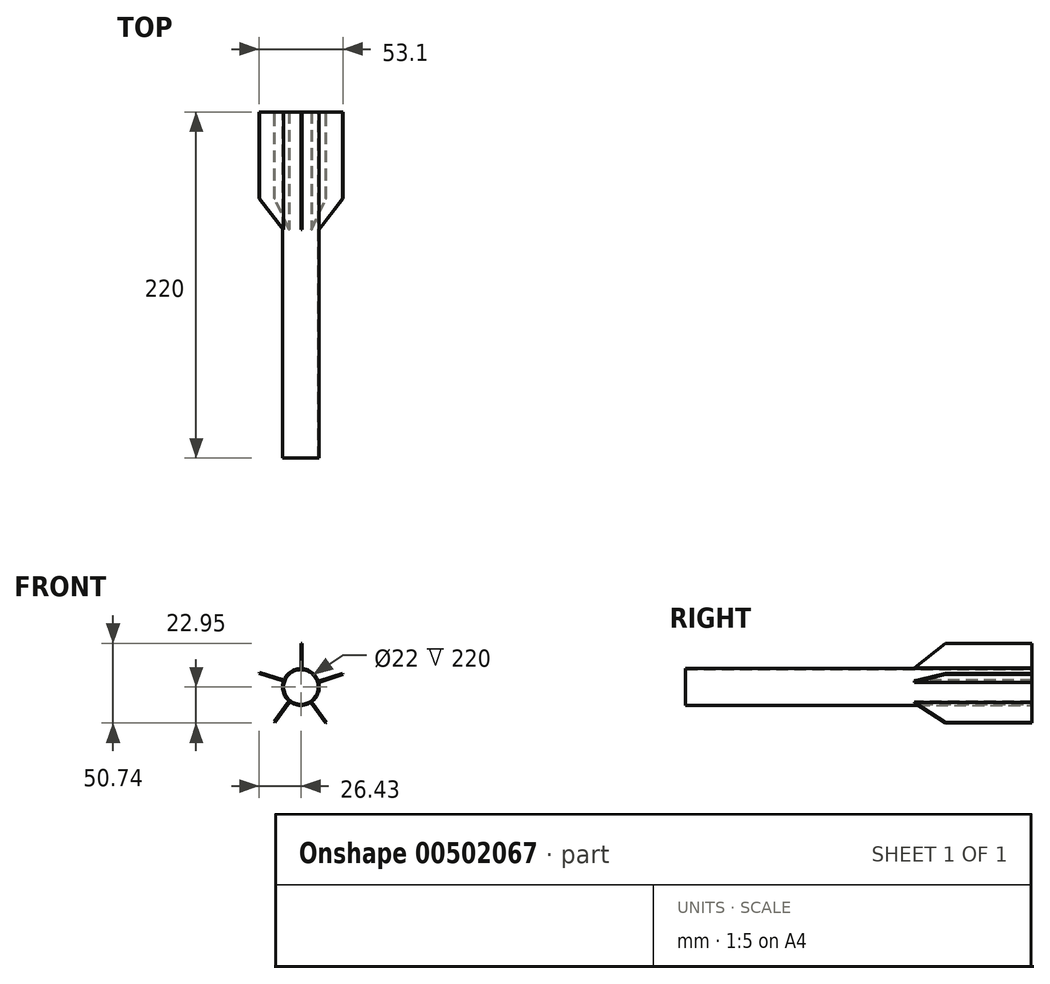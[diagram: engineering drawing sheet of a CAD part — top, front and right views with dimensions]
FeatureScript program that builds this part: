
annotation { "Feature Type Name" : "Feature", "Feature Type Description" : "" }
export const myFeature = defineFeature(function(context is Context, id is Id, definition is map)
    precondition{}
    {
        {
            var Q0;
            Q0=qCreatedBy(makeId("Front.planeOp"),FACE);
            var sketch = newSketch(context, id + "F0", { "sketchPlane" : qUnion([Q0])});
            skCircle(sketch, "E0", {"center": v(0, 0) * mm, "radius": 11.65 * mm});
            skCircle(sketch, "E1", {"center": v(0, 0) * mm, "radius": 11 * mm});
            skSolve(sketch);
        }
        {
            var Q0;
            Q0=makeQuery(id+"F0.imprint","IMPRINT",FACE,{"disambiguationData":[TD([[makeQuery(id+"F0.imprint","IMPRINT",EDGE,{"derivedFrom":sQuery(id+"F0.wireOp",EDGE,"E0")}),1.0]])]});
            extrude(context, id + "F1", {"entities" : qUnion([Q0]), "depth" : 220 * mm});
        }
        {
            var Q0;
            Q0=qCreatedBy(makeId("Right.planeOp"),FACE);
            var sketch = newSketch(context, id + "F2", { "sketchPlane" : qUnion([Q0])});
            skLineSegment(sketch, "E2", {"start": v(0, 11.98) * mm, "end": v(-74.69, 11.98) * mm});
            skLineSegment(sketch, "E3", {"start": v(-74.69, 11.98) * mm, "end": v(-55, 27.79) * mm});
            skLineSegment(sketch, "E4", {"start": v(-55, 27.79) * mm, "end": v(0, 27.79) * mm});
            skLineSegment(sketch, "E5", {"start": v(0, 27.79) * mm, "end": v(0, 11.98) * mm});
            skSolve(sketch);
        }
        {
            var Q0;
            Q0 = qSketchRegion(id + "F2", true);
            extrude(context, id + "F3", {"entities" : qUnion([Q0]), "depth" : 0.8 * mm});
        }
        {
            var Q0;
            Q0=makeQuery(id+"F3.opExtrude","SWEPT_BODY",BODY,{"disambiguationData":[OSD([sQuery(id+"F2.wireOp",EDGE,"E2"),sQuery(id+"F2.wireOp",EDGE,"E3"),sQuery(id+"F2.wireOp",EDGE,"E4"),sQuery(id+"F2.wireOp",EDGE,"E5")])]});
            var Q1;
            Q1=makeQuery(id+"F1.opExtrude","SWEPT_FACE",FACE,{"disambiguationData":[OSD([sQuery(id+"F0.wireOp",EDGE,"E0")])]});
            circularPattern(context, id + "F4", {"operationType" : NewBodyOperationType.ADD, "entities" : qUnion([Q0]), "axis" : qUnion([Q1]), "angle" : 360 * degree, "instanceCount" : 5, "equalSpace" : true});
        }
    });
